# Revit family: Plumbing_Fixtures_Grohe_Eurocube_OHM_Basin_Mixer_(M)_23445000-14-METRIC1
name_source: partatom
category: Plumbing Fixtures
revit_build: Autodesk Revit 2014 (Build: 20130308_1515(x64)
units: mm (PartAtom-declared; Revit-internal decimal feet)

## types (1)
- Plumbing_Fixtures_Grohe_Eurocube_OHM_Basin_Mixer_(M)_23445000-14-METRIC1
    Assembly Code = C1030220
    AssetType = Fixed
    CW Connection = Yes
    CWFU = 0
    ClassificationName = Uniclass 2015
    ClassificationValue = Pr_40_20_87_98
    Color = Chrome
    Cost = 0 $
    Default Elevation = 600 mm
    Description = Single Lever Basin Mixer Meduim Size
    DocumentationCertificates = http://www.grohe.com
    DocumentationInstallationGuide = http://cdn08.grohe.com
    DocumentationLiterature = http://cdn08.grohe.com
    DocumentationTechnical = http://cdn08.grohe.com
    DurationUnit = Years
    ExpectedLife = 0
    Faucet Material = Grohe-Chrome
    Finish = Chrome
    HW Connection = Yes
    HWFU = 0
    Height = 172 mm  [stored 0.564304 ft]
    Keynote = N13
    Low Emitting Material = No
    Manufacturer = Grohe
    Material = Chrome
    Model = Eurocube OHM - Single Lever Basin Mixer Meduim Size - 2344500
    ModelNumber = 23445000
    NBSDescription = Water supply fittings for wash basins and troughs
    NBSObjectName = Washbasin taps
    NBSReference = 45-35-70/371
    Name = Eurocube OHM - Single Lever Basin Mixer Meduim Size - 2344500
    Type Comments = Single Lever Basin Mixer Meduim Size
    TypeName = Eurocube OHM - Single Lever Basin Mixer Meduim Size - 2344500
    URL = www.grohe.com
    Vent Connection = No
    WFU = 0
    WarrantyDurationUnit = Years
    Waste Connection = No
    Width = 133 mm  [stored 0.436352 ft]
    _BIMspec_GUID = 0
    _current revision = 1
    _distributed by = www.bimstore.co.uk

note: [stored X ft] marks values corroborated as IEEE doubles in the binary element streams (Revit-internal decimal feet)

## geometry (parser evidence)
native form markers: Blend x6, Sweep x1
no freeform markers — native parametric forms only
